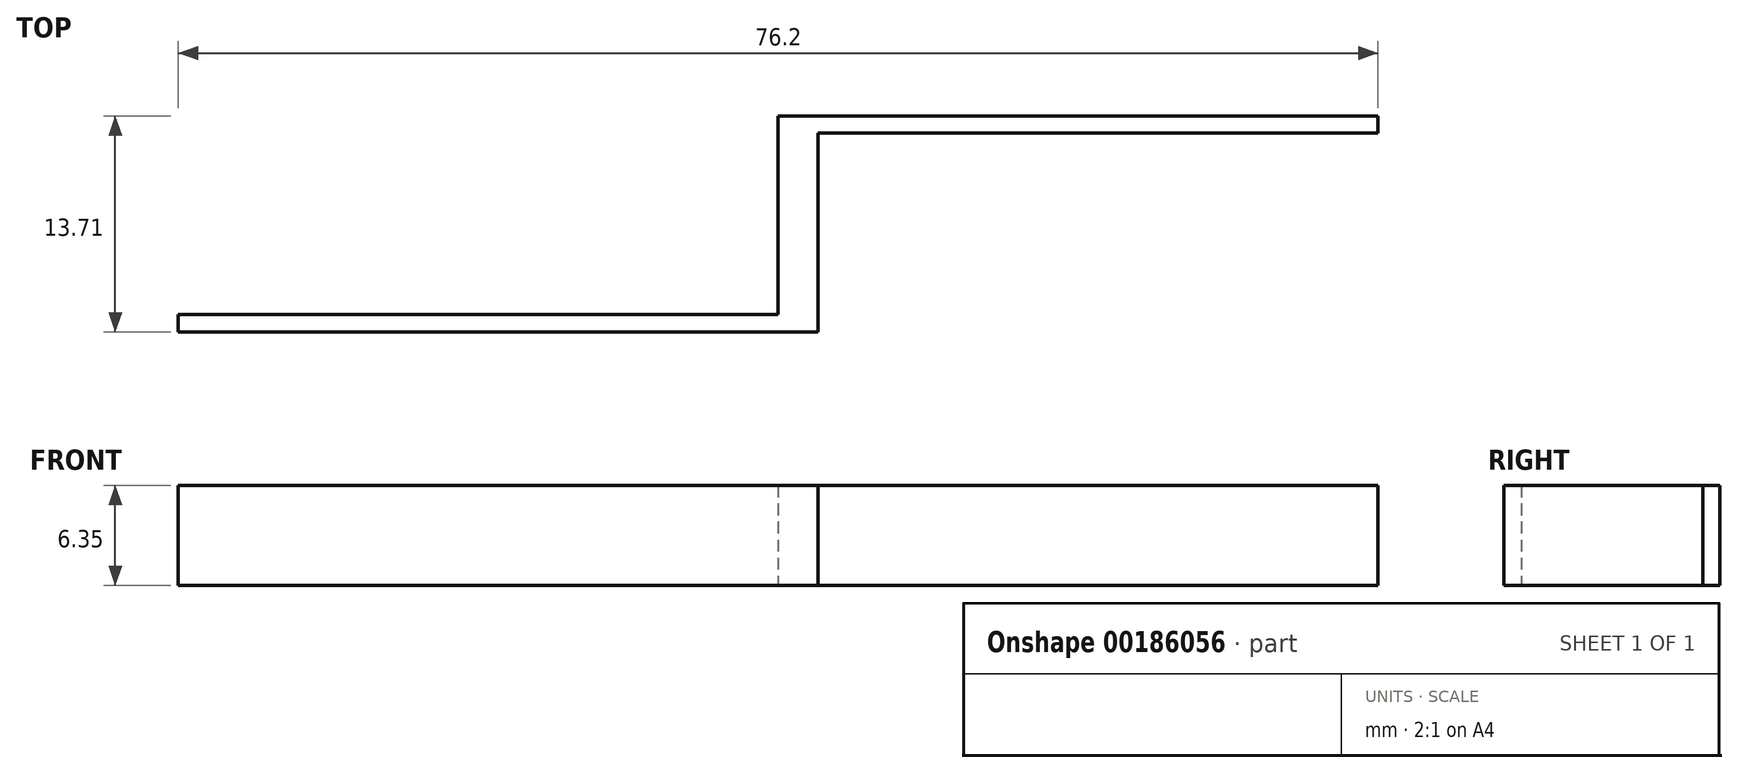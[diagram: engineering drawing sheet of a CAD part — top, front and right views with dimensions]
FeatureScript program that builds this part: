
annotation { "Feature Type Name" : "Feature", "Feature Type Description" : "" }
export const myFeature = defineFeature(function(context is Context, id is Id, definition is map)
    precondition{}
    {
        {
            var Q0;
            Q0=qCreatedBy(makeId("Top.planeOp"),FACE);
            var sketch = newSketch(context, id + "F0", { "sketchPlane" : qUnion([Q0])});
            skLineSegment(sketch, "E0.bottom", {"start": v(0, 0) * mm, "end": v(40.64, 0) * mm});
            skLineSegment(sketch, "E0.top", {"start": v(0, 1.1) * mm, "end": v(38.1, 1.1) * mm});
            skLineSegment(sketch, "E0.left", {"start": v(0, 0) * mm, "end": v(0, 1.1) * mm});
            skLineSegment(sketch, "E1.right", {"start": v(38.1, 1.1) * mm, "end": v(38.1, 12.62) * mm});
            skLineSegment(sketch, "E2.bottom", {"start": v(40.64, 12.62) * mm, "end": v(76.2, 12.62) * mm});
            skLineSegment(sketch, "E2.top", {"start": v(38.1, 13.71) * mm, "end": v(76.2, 13.71) * mm});
            skLineSegment(sketch, "E2.left", {"start": v(38.1, 12.62) * mm, "end": v(38.1, 13.71) * mm});
            skLineSegment(sketch, "E2.right", {"start": v(76.2, 12.62) * mm, "end": v(76.2, 13.71) * mm});
            skLineSegment(sketch, "E3", {"start": v(40.64, 12.62) * mm, "end": v(40.64, 0) * mm});
            skSolve(sketch);
        }
        {
            var Q0;
            Q0 = qSketchRegion(id + "F0", true);
            extrude(context, id + "F1", {"entities" : qUnion([Q0]), "depth" : 6.35 * mm});
        }
    });
